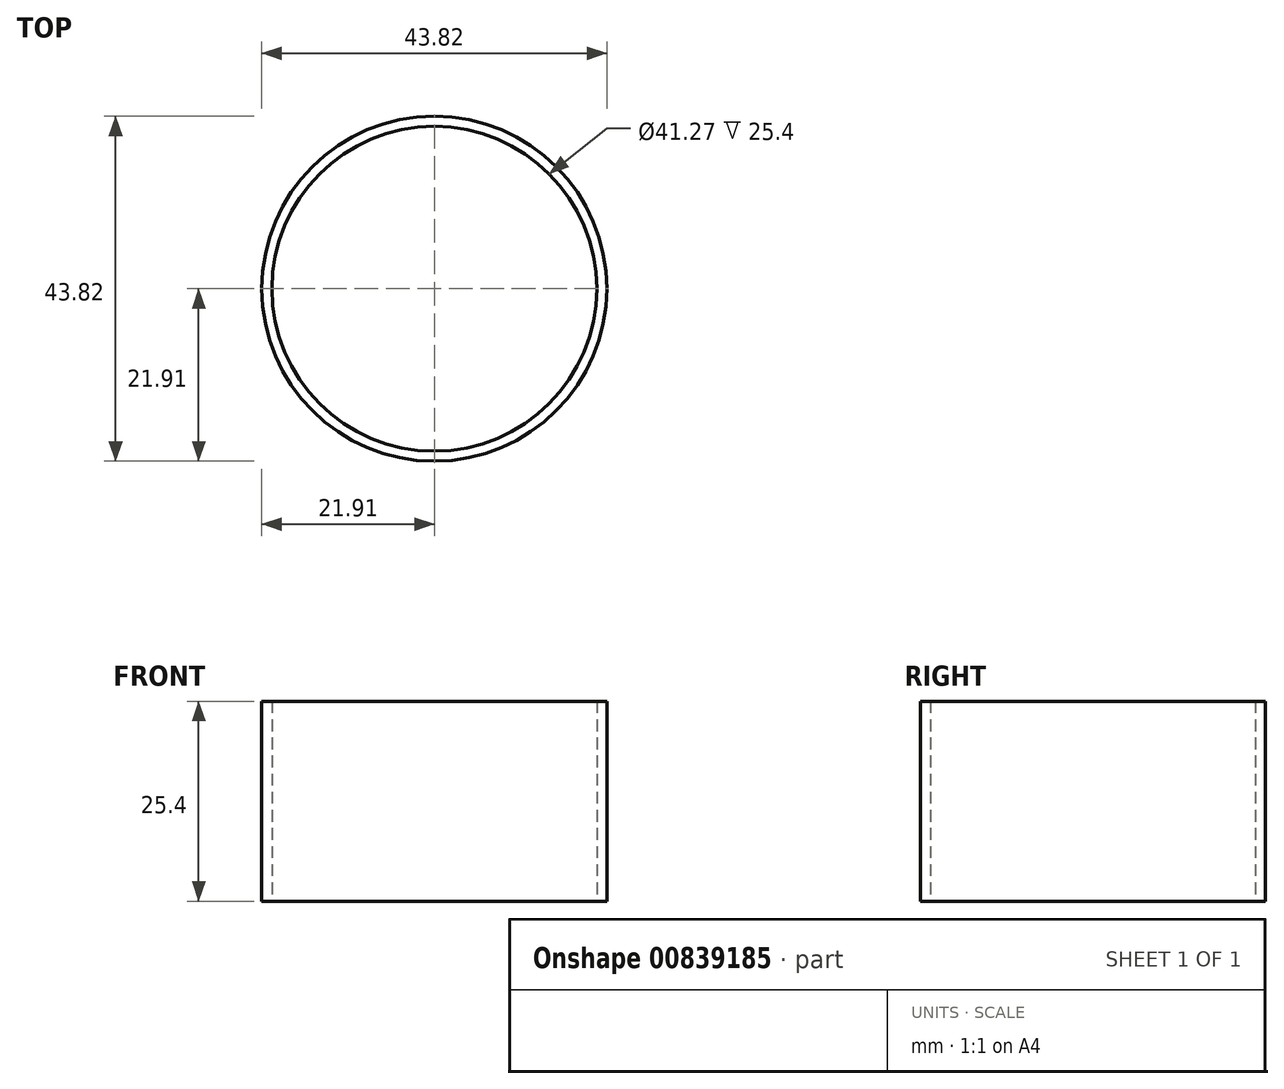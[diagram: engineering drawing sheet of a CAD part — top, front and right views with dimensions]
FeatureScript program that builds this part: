
annotation { "Feature Type Name" : "Feature", "Feature Type Description" : "" }
export const myFeature = defineFeature(function(context is Context, id is Id, definition is map)
    precondition{}
    {
        {
            var Q0;
            Q0=qCreatedBy(makeId("Top.planeOp"),FACE);
            var sketch = newSketch(context, id + "F0", { "sketchPlane" : qUnion([Q0])});
            skCircle(sketch, "E0", {"center": v(0, 0) * mm, "radius": 20.64 * mm});
            skCircle(sketch, "E1", {"center": v(0, 0) * mm, "radius": 21.9 * mm});
            skSolve(sketch);
        }
        {
            var Q0;
            Q0=makeQuery(id+"F0.imprint","IMPRINT",FACE,{"disambiguationData":[TD([[makeQuery(id+"F0.imprint","IMPRINT",EDGE,{"derivedFrom":sQuery(id+"F0.wireOp",EDGE,"E0")}),-1.0]])]});
            extrude(context, id + "F1", {"entities" : qUnion([Q0]), "depth" : 25.4 * mm, "offsetDistance" : 25.4 * mm});
        }
    });
